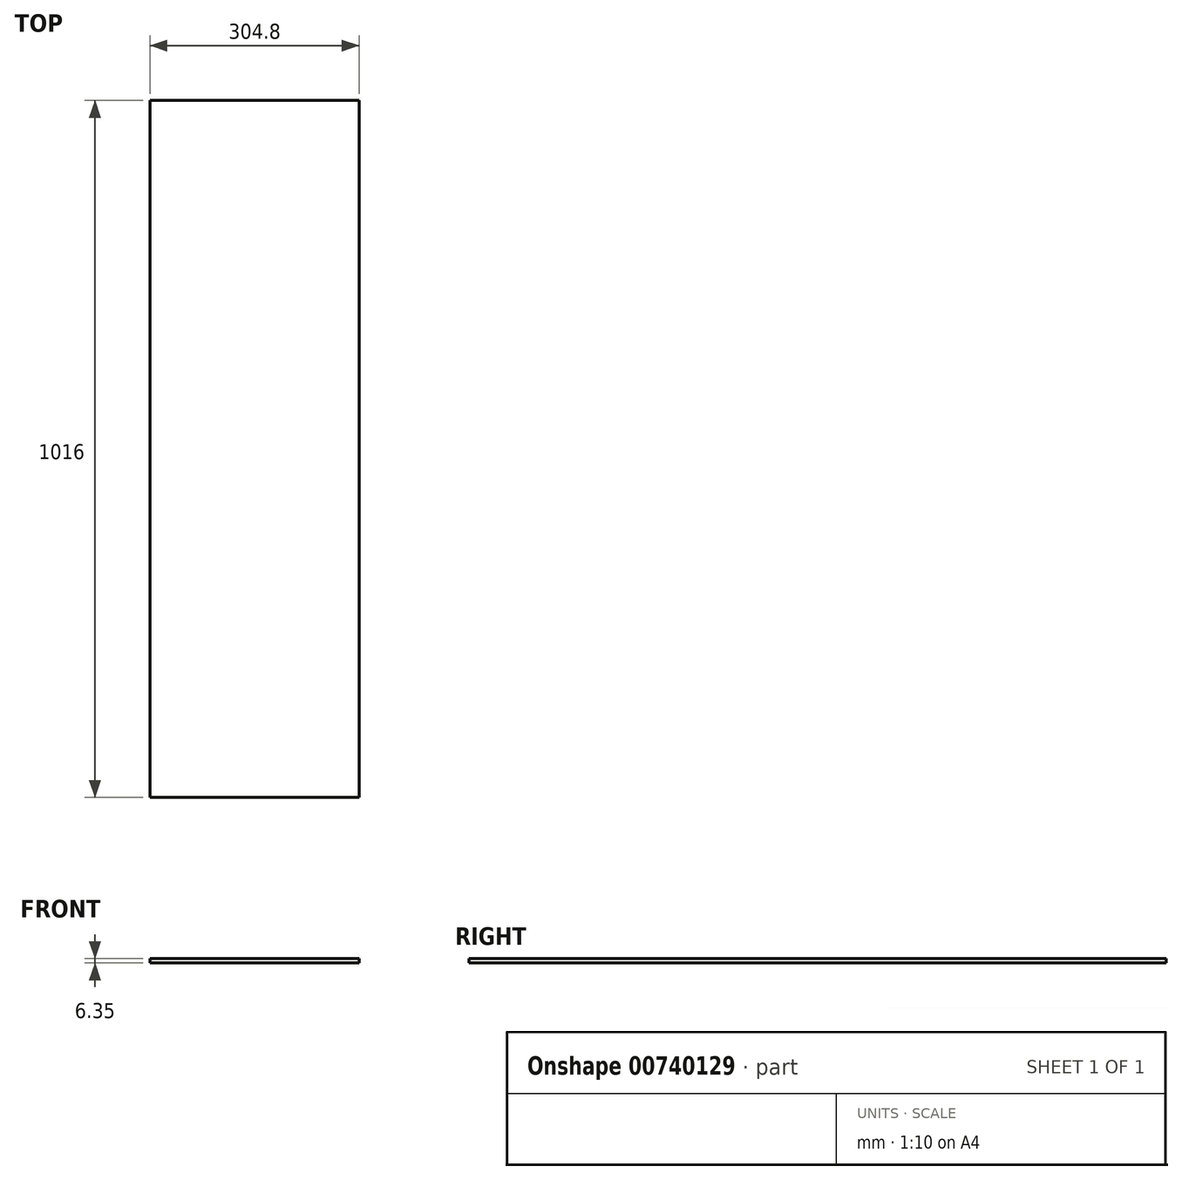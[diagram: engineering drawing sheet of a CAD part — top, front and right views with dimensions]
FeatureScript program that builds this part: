
annotation { "Feature Type Name" : "Feature", "Feature Type Description" : "" }
export const myFeature = defineFeature(function(context is Context, id is Id, definition is map)
    precondition{}
    {
        {
            var Q0;
            Q0=qCreatedBy(makeId("Top.planeOp"),FACE);
            var sketch = newSketch(context, id + "F0", { "sketchPlane" : qUnion([Q0])});
            skLineSegment(sketch, "E0.bottom", {"start": v(327.1, -203.66) * mm, "end": v(22.3, -203.66) * mm});
            skLineSegment(sketch, "E0.top", {"start": v(327.1, 812.34) * mm, "end": v(22.3, 812.34) * mm});
            skLineSegment(sketch, "E0.left", {"start": v(327.1, -203.66) * mm, "end": v(327.1, 812.34) * mm});
            skLineSegment(sketch, "E0.right", {"start": v(22.3, -203.66) * mm, "end": v(22.3, 812.34) * mm});
            skSolve(sketch);
        }
        {
            var Q0;
            Q0=makeQuery(id+"F0.imprint","IMPRINT",FACE,{"disambiguationData":[TD([[makeQuery(id+"F0.imprint","IMPRINT",EDGE,{"derivedFrom":sQuery(id+"F0.wireOp",EDGE,"E0.right")}),1.0]])]});
            var Q1;
            Q1=makeQuery(id+"F0.imprint","IMPRINT",FACE,{"disambiguationData":[TD([[makeQuery(id+"F0.imprint","IMPRINT",EDGE,{"derivedFrom":sQuery(id+"F0.wireOp",EDGE,"E0.bottom")}),-1.0]])]});
            extrude(context, id + "F1", {"entities" : qUnion([Q0, Q1]), "depth" : 6.35 * mm, "offsetDistance" : 25.4 * mm});
        }
    });
